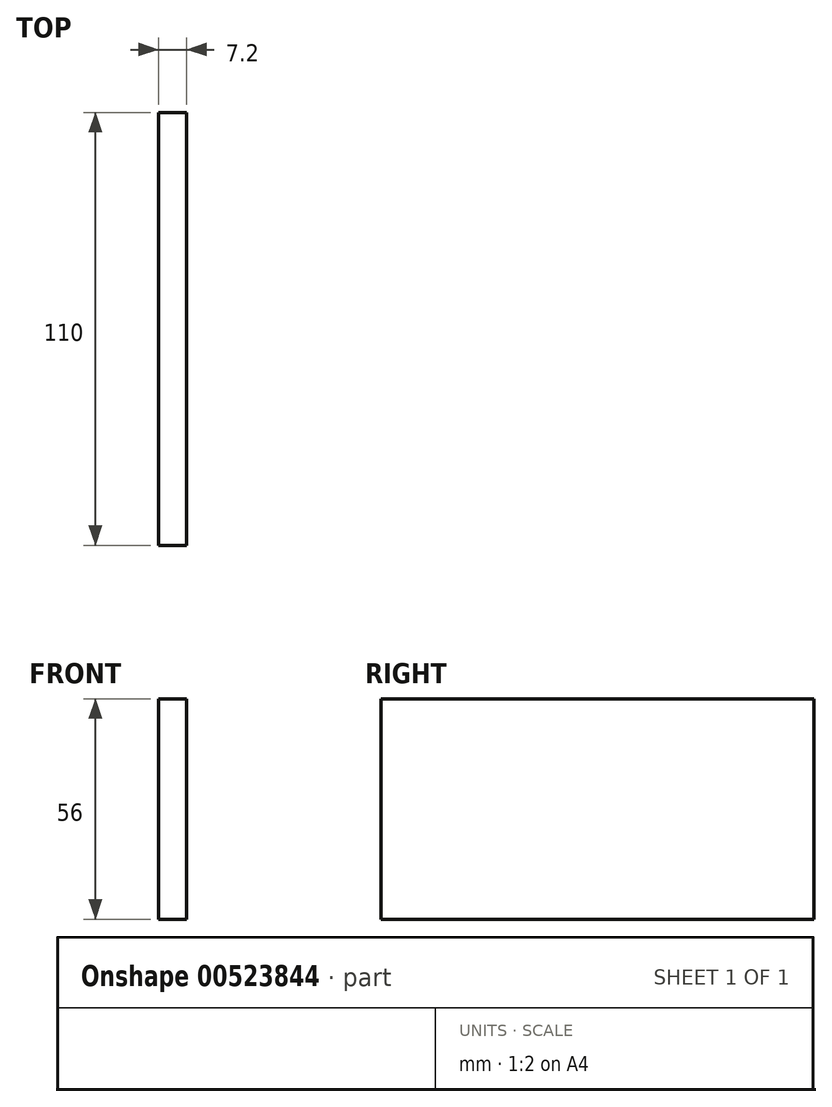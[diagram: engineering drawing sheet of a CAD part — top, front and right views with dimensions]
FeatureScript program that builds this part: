
annotation { "Feature Type Name" : "Feature", "Feature Type Description" : "" }
export const myFeature = defineFeature(function(context is Context, id is Id, definition is map)
    precondition{}
    {
        {
            var Q0;
            Q0=qCreatedBy(makeId("Right.planeOp"),FACE);
            var sketch = newSketch(context, id + "F0", { "sketchPlane" : qUnion([Q0])});
            skLineSegment(sketch, "E0.bottom", {"start": v(-55, 28) * mm, "end": v(55, 28) * mm});
            skLineSegment(sketch, "E0.top", {"start": v(-55, -28) * mm, "end": v(55, -28) * mm});
            skLineSegment(sketch, "E0.left", {"start": v(-55, 28) * mm, "end": v(-55, -28) * mm});
            skLineSegment(sketch, "E0.right", {"start": v(55, 28) * mm, "end": v(55, -28) * mm});
            skPoint(sketch, "E0.middle", {"position": v(0, 0) * mm});
            skSolve(sketch);
        }
        {
            var Q0;
            Q0=makeQuery(id+"F0.imprint","IMPRINT",FACE,{"disambiguationData":[TD([[makeQuery(id+"F0.imprint","IMPRINT",EDGE,{"derivedFrom":sQuery(id+"F0.wireOp",EDGE,"E0.bottom")}),-1.0]])]});
            extrude(context, id + "F1", {"entities" : qUnion([Q0]), "endBound" : BoundingType.SYMMETRIC, "depth" : 7.2 * mm, "offsetDistance" : 25 * mm});
        }
    });
